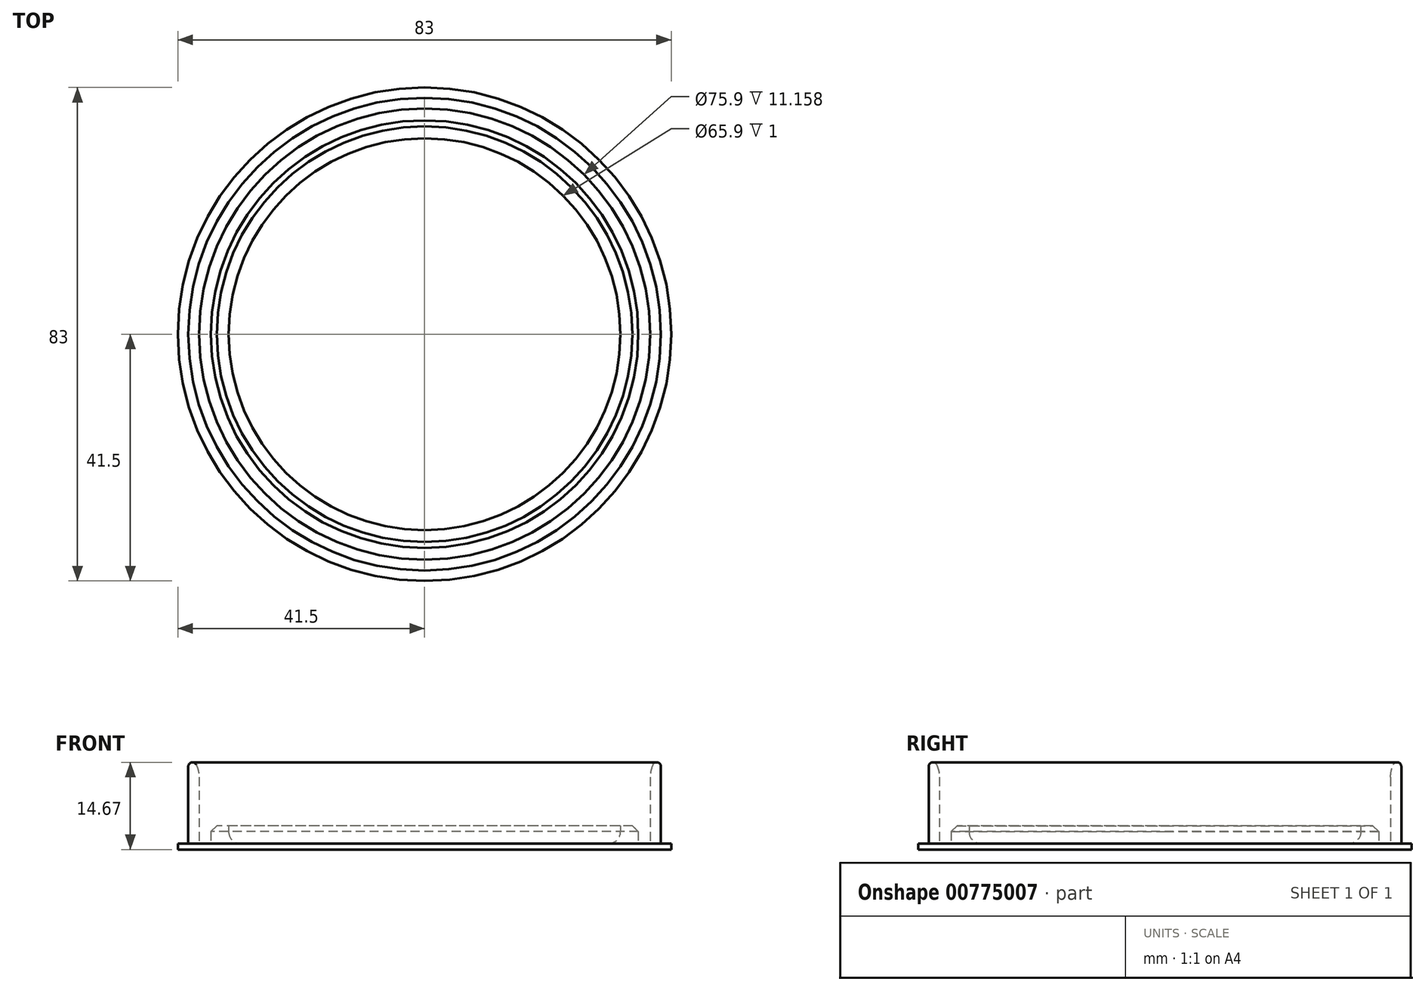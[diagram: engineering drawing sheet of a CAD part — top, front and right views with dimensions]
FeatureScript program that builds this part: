
annotation { "Feature Type Name" : "Feature", "Feature Type Description" : "" }
export const myFeature = defineFeature(function(context is Context, id is Id, definition is map)
    precondition{}
    {
        {
            var Q0;
            Q0=qCreatedBy(makeId("Top.planeOp"),FACE);
            var sketch = newSketch(context, id + "F0", { "sketchPlane" : qUnion([Q0])});
            skCircle(sketch, "E0", {"center": v(0, 0) * mm, "radius": 41.5 * mm});
            skSolve(sketch);
        }
        {
            var Q0;
            Q0=makeQuery(id+"F0.imprint","IMPRINT",FACE,{"disambiguationData":[TD([[makeQuery(id+"F0.imprint","IMPRINT",EDGE,{"derivedFrom":sQuery(id+"F0.wireOp",EDGE,"E0")}),1.0]])]});
            extrude(context, id + "F1", {"entities" : qUnion([Q0]), "depth" : 1 * mm, "offsetDistance" : 25 * mm});
        }
        {
            var Q0;
            Q0=makeQuery(id+"F1.opExtrude","CAP_FACE",FACE,{"disambiguationData":[OSD([sQuery(id+"F0.wireOp",EDGE,"E0")])],"isStart":false});
            var sketch = newSketch(context, id + "F2", { "sketchPlane" : qUnion([Q0])});
            skCircle(sketch, "E1", {"center": v(0, 0) * mm, "radius": 39.75 * mm});
            skCircle(sketch, "E2", {"center": v(0, 0) * mm, "radius": 37.95 * mm});
            skSolve(sketch);
        }
        {
            var Q0;
            Q0=makeQuery(id+"F2.imprint","IMPRINT",FACE,{"disambiguationData":[TD([[makeQuery(id+"F2.imprint","IMPRINT",EDGE,{"derivedFrom":sQuery(id+"F2.wireOp",EDGE,"E1")}),1.0]])]});
            extrude(context, id + "F3", {"entities" : qUnion([Q0]), "operationType" : NewBodyOperationType.ADD, "depth" : 15 * mm, "offsetDistance" : 25 * mm});
        }
        {
            var Q0;
            Q0=makeQuery(id+"F3.boolean.opBoolean","SPLIT",FACE,{"disambiguationData":[TD([makeQuery(id+"F3.opExtrude","SWEPT_FACE",FACE,{"disambiguationData":[OSD([sQuery(id+"F2.wireOp",EDGE,"E2")])]})])],"derivedFrom":makeQuery(id+"F1.opExtrude","CAP_FACE",FACE,{"disambiguationData":[OSD([sQuery(id+"F0.wireOp",EDGE,"E0")])],"isStart":false})});
            var sketch = newSketch(context, id + "F4", { "sketchPlane" : qUnion([Q0])});
            skCircle(sketch, "E3", {"center": v(0, 0) * mm, "radius": 35.95 * mm});
            skCircle(sketch, "E4", {"center": v(0, 0) * mm, "radius": 32.95 * mm});
            skSolve(sketch);
        }
        {
            var Q0;
            Q0=makeQuery(id+"F4.imprint","IMPRINT",FACE,{"disambiguationData":[TD([[makeQuery(id+"F4.imprint","IMPRINT",EDGE,{"derivedFrom":sQuery(id+"F4.wireOp",EDGE,"E3")}),1.0]])]});
            extrude(context, id + "F5", {"entities" : qUnion([Q0]), "operationType" : NewBodyOperationType.ADD, "depth" : 3 * mm, "offsetDistance" : 25 * mm});
        }
        {
            var Q0;
            Q0=makeQuery(id+"F5.opExtrude","CAP_EDGE",EDGE,{"disambiguationData":[OSD([sQuery(id+"F4.wireOp",EDGE,"E3")])],"isStart":false});
            chamfer(context, id + "F6", {"entities" : qUnion([Q0]), "width" : 1 * mm, "tangentPropagation" : true});
        }
        {
            var Q0;
            Q0=makeQuery(id+"F3.opExtrude","CAP_EDGE",EDGE,{"disambiguationData":[OSD([sQuery(id+"F2.wireOp",EDGE,"E2")])],"isStart":false});
            fillet(context, id + "F7", {"entities" : qUnion([Q0]), "radius" : 5 * mm, "tangentPropagation" : true, "allowEdgeOverflow" : false});
        }
        {
            var Q0;
            Q0=makeQuery(id+"F7.opFillet","BLEND_EDGE",EDGE,{"blendedFrom":[makeQuery(id+"F3.opExtrude","CAP_EDGE",EDGE,{"disambiguationData":[OSD([sQuery(id+"F2.wireOp",EDGE,"E2")])],"isStart":false}),makeQuery(id+"F3.opExtrude","SWEPT_FACE",FACE,{"disambiguationData":[OSD([sQuery(id+"F2.wireOp",EDGE,"E1")])]})],"blendedInto":[makeQuery(id+"F3.opExtrude","SWEPT_FACE",FACE,{"disambiguationData":[OSD([sQuery(id+"F2.wireOp",EDGE,"E1")])]})]});
            fillet(context, id + "F8", {"entities" : qUnion([Q0]), "radius" : 0.7 * mm, "tangentPropagation" : true, "allowEdgeOverflow" : false});
        }
        {
            var Q0;
            Q0=makeQuery(id+"F5.opExtrude","CAP_EDGE",EDGE,{"disambiguationData":[OSD([sQuery(id+"F4.wireOp",EDGE,"E4")])],"isStart":true});
            fillet(context, id + "F9", {"entities" : qUnion([Q0]), "radius" : 2 * mm, "tangentPropagation" : true, "allowEdgeOverflow" : false});
        }
    });
